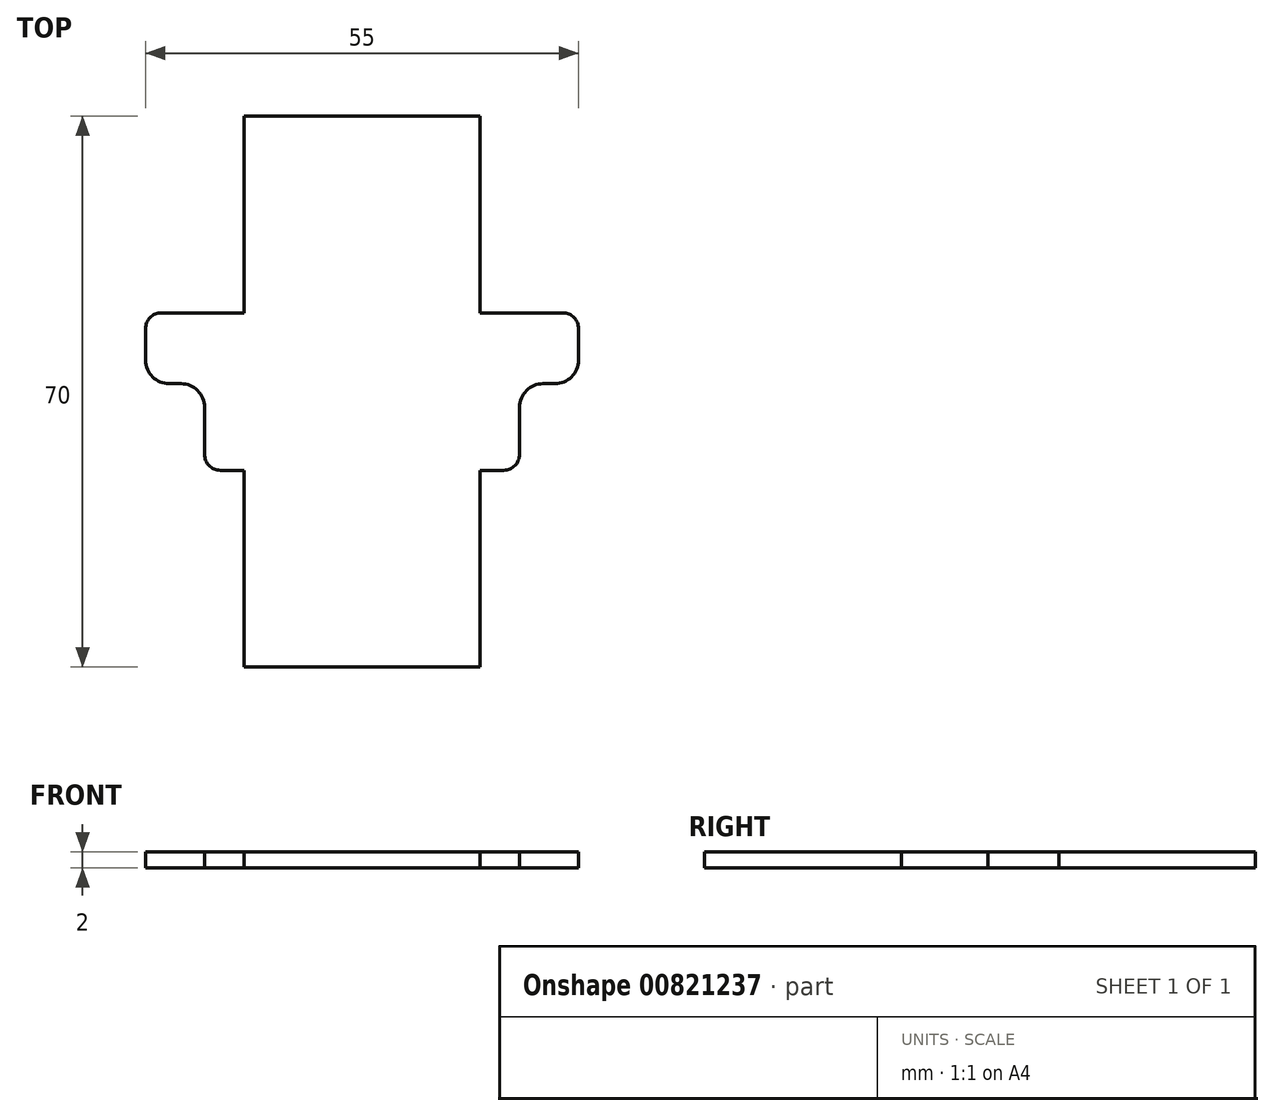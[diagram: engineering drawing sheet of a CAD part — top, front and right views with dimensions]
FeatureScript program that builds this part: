
annotation { "Feature Type Name" : "Feature", "Feature Type Description" : "" }
export const myFeature = defineFeature(function(context is Context, id is Id, definition is map)
    precondition{}
    {
        {
            var Q0;
            Q0=qCreatedBy(makeId("Top.planeOp"),FACE);
            var sketch = newSketch(context, id + "F0", { "sketchPlane" : qUnion([Q0])});
            skLineSegment(sketch, "E0.bottom", {"start": v(-15, -35) * mm, "end": v(15, -35) * mm});
            skLineSegment(sketch, "E0.top", {"start": v(-15, 35) * mm, "end": v(15, 35) * mm});
            skLineSegment(sketch, "E0.left", {"start": v(-15, -35) * mm, "end": v(-15, -10) * mm});
            skLineSegment(sketch, "E0.right", {"start": v(15, -35) * mm, "end": v(15, -10) * mm});
            skPoint(sketch, "E0.middle", {"position": v(0, 0) * mm});
            skLineSegment(sketch, "E1", {"start": v(-15, 10) * mm, "end": v(-25.5, 10) * mm});
            skLineSegment(sketch, "E2", {"start": v(-15, -10) * mm, "end": v(-18, -10) * mm});
            skLineSegment(sketch, "E3.MirrorCS", {"start": v(15, 10) * mm, "end": v(25.5, 10) * mm});
            skLineSegment(sketch, "E4.MirrorCS", {"start": v(15, -10) * mm, "end": v(18, -10) * mm});
            skLineSegment(sketch, "E5", {"start": v(-27.5, 4) * mm, "end": v(-27.5, 8) * mm});
            skPoint(sketch, "E5.endSnap0", {"position": v(-28.29, 10) * mm});
            skLineSegment(sketch, "E6.MirrorCS", {"start": v(27.5, 4) * mm, "end": v(27.5, 8) * mm});
            skPoint(sketch, "E7.orphan", {"position": v(-41.58, 10) * mm});
            skPoint(sketch, "E8.orphan", {"position": v(-40.92, -10) * mm});
            skLineSegment(sketch, "E9.trimOffspring", {"start": v(-15, 10) * mm, "end": v(-15, 35) * mm});
            skPoint(sketch, "E10.orphan", {"position": v(41.58, 10) * mm});
            skPoint(sketch, "E11.orphan", {"position": v(40.92, -10) * mm});
            skLineSegment(sketch, "E12.trimOffspring", {"start": v(15, 10) * mm, "end": v(15, 35) * mm});
            skLineSegment(sketch, "E13", {"start": v(-24.5, 1) * mm, "end": v(-23, 1) * mm});
            skLineSegment(sketch, "E14", {"start": v(-20, -2) * mm, "end": v(-20, -8) * mm});
            skPoint(sketch, "E14.endSnap0", {"position": v(-21.25, -10) * mm});
            skPoint(sketch, "E15.orphan", {"position": v(-27.5, -10) * mm});
            skLineSegment(sketch, "E16.MirrorCS", {"start": v(24.5, 1) * mm, "end": v(23, 1) * mm});
            skLineSegment(sketch, "E17.MirrorCS", {"start": v(20, -2) * mm, "end": v(20, -8) * mm});
            skPoint(sketch, "E18.orphan", {"position": v(27.5, -10) * mm});
            skPoint(sketch, "E19.newPointB", {"position": v(-27.5, 10) * mm});
            skArc(sketch, "E19.filletArc", {"start": v(-25.5, 10) * mm, "mid": v(-26.91, 9.41) * mm, "end": v(-27.5, 8) * mm});
            skPoint(sketch, "E20.visualSharp", {"position": v(27.5, 10) * mm});
            skArc(sketch, "E20.filletArc", {"start": v(27.5, 8) * mm, "mid": v(26.91, 9.41) * mm, "end": v(25.5, 10) * mm});
            skPoint(sketch, "E21.visualSharp", {"position": v(-27.5, 1) * mm});
            skArc(sketch, "E21.filletArc", {"start": v(-27.5, 4) * mm, "mid": v(-26.62, 1.88) * mm, "end": v(-24.5, 1) * mm});
            skPoint(sketch, "E22.visualSharp", {"position": v(-20, 1) * mm});
            skArc(sketch, "E22.filletArc", {"start": v(-20, -2) * mm, "mid": v(-20.88, 0.12) * mm, "end": v(-23, 1) * mm});
            skArc(sketch, "E23.MirrorCS", {"start": v(27.5, 4) * mm, "mid": v(26.62, 1.88) * mm, "end": v(24.5, 1) * mm});
            skArc(sketch, "E24.MirrorCS", {"start": v(20, -2) * mm, "mid": v(20.88, 0.12) * mm, "end": v(23, 1) * mm});
            skPoint(sketch, "E25.orphan", {"position": v(27.5, 1) * mm});
            skPoint(sketch, "E26.orphan", {"position": v(20, 1) * mm});
            skPoint(sketch, "E27.newPointA", {"position": v(-20, -10) * mm});
            skArc(sketch, "E27.filletArc", {"start": v(-20, -8) * mm, "mid": v(-19.41, -9.41) * mm, "end": v(-18, -10) * mm});
            skPoint(sketch, "E28.visualSharp", {"position": v(20, -10) * mm});
            skArc(sketch, "E28.filletArc", {"start": v(18, -10) * mm, "mid": v(19.41, -9.41) * mm, "end": v(20, -8) * mm});
            skSolve(sketch);
        }
        {
            var Q0;
            Q0 = qSketchRegion(id + "F0", true);
            extrude(context, id + "F1", {"entities" : qUnion([Q0]), "depth" : 2 * mm, "offsetDistance" : 25 * mm});
        }
    });
